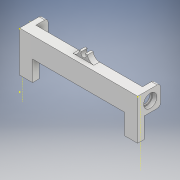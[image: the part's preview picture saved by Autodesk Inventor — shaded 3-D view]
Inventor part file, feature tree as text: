
AUTODESK INVENTOR PART (.ipt)
format: ipt  version: 2018 (Build 220112000, 112)  size: 1,079,296 bytes
history: native  units: mm
features: sketch x60, extrude x49, fillet x5
ambient origin geometry x8: Origin, YZ Plane, XZ Plane, XY Plane, X Axis, Y Axis, Z Axis, Center Point
bodies: Solid1 (feature_tree)
feature tree (114):
  extrude  "Extrusion1"  Depth=80.0mm
  extrude  "Extrusion2"  Depth=3.0mm
  sketch  "Sketch3"  dims[d5=12.0mm d6=14.5mm]
  extrude  "Extrusion3"  Depth=14.5mm
  extrude  "Extrusion4"  Depth=2.0mm
  extrude  "Extrusion5"  Depth=0.5mm TaperAngle=0.0deg
  sketch  "Sketch7"  dims[d15=10.0mm d16=25.0mm]
  extrude  "Extrusion6"  Depth=25.0mm
  extrude  "Extrusion7"  Depth=25.0mm
  extrude  "Extrusion8"  Depth=10.0mm
  fillet  "Fillet1"  Radius=10.0mm
  fillet  "Fillet2"  Radius=10.0mm
  extrude  "Extrusion9"  Depth=2.5mm TaperAngle=0.0deg
  extrude  "Extrusion10"  Depth=4.0mm
  fillet  "Fillet3"  Radius=3.0mm
  extrude  "Extrusion11"  Depth=21.0mm
  extrude  "Extrusion12"  Depth=41.0mm
  extrude  "Extrusion13"  Depth=42.0mm
  extrude  "Extrusion14"  Depth=38.0mm
  extrude  "Extrusion15"  Depth=45.0mm TaperAngle=0.0deg
  extrude  "Extrusion16"  Depth=3.0mm TaperAngle=0.0deg
  extrude  "Extrusion17"  Depth=3.0mm
  extrude  "Extrusion18"  Depth=39.5mm
  extrude  "Extrusion19"  Depth=7.25mm
  extrude  "Extrusion20"  Depth=7.75mm
  extrude  "Extrusion21"  Depth=10.0mm
  sketch  "Sketch24"  dims[d65=66.0mm d66=3.5mm d67=0.0mm]
  extrude  "Extrusion22"  Depth=10.0mm TaperAngle=0.0deg
  extrude  "Extrusion23"  Depth=16.0mm
  extrude  "Extrusion24"  Depth=3.5mm TaperAngle=0.0deg
  extrude  "Extrusion25"  Depth=2.0mm
  extrude  "Extrusion26"  Depth=2.0mm TaperAngle=0.0deg
  sketch  "Sketch30"  dims[d81=4.0mm d82=4.0mm]
  extrude  "Extrusion27"  Depth=16.0mm
  extrude  "Extrusion28"  Depth=2.0mm
  extrude  "Extrusion29"  Depth=3.5mm TaperAngle=0.0deg
  sketch  "Sketch34"  dims[d91=5.0mm d92=16.0mm d93=5.0mm]
  extrude  "Extrusion30"  Depth=4.0mm
  extrude  "Extrusion31"  Depth=2.0mm TaperAngle=0.0deg
  extrude  "Extrusion32"  Depth=150.0mm TaperAngle=0.0deg
  sketch  "Sketch38"  dims[d102=5.0mm d103=0.0mm d104=500.0mm d105=0.0mm]
  extrude  "Extrusion33"  Depth=16.0mm
  sketch  "Sketch40"  dims[d110=38.75mm d111=38.75mm]
  extrude  "Extrusion34"  Depth=16.0mm
  fillet  "Fillet4"  Radius=5.0mm
  extrude  "Extrusion35"  Depth=3.0mm
  extrude  "Extrusion36"  Depth=43.0mm TaperAngle=0.0deg
  extrude  "Extrusion37"  Depth=38.75mm
  extrude  "Extrusion38"  Depth=5.0mm TaperAngle=0.0deg
  extrude  "Extrusion39"  Depth=45.0mm TaperAngle=0.0deg
  extrude  "Extrusion40"  Depth=38.75mm
  sketch  "Sketch48"  dims[d134=16.0mm d135=5.0mm d136=0.0mm d137=7.0mm]
  extrude  "Extrusion41"  Depth=3.5mm TaperAngle=0.0deg
  extrude  "Extrusion42"  Depth=100.0mm TaperAngle=0.0deg
  extrude  "Extrusion43"  Depth=1.5mm TaperAngle=0.0deg
  sketch  "Sketch52"  dims[d144=16.0mm]
  extrude  "Extrusion44"  Depth=10.0mm
  extrude  "Extrusion45"  Depth=10.0mm
  extrude  "Extrusion46"  Depth=7.0mm
  sketch  "Sketch56"  dims[d150=5.0mm d151=0.0mm]
  sketch  "Sketch57"  dims[d152=5.0mm d153=0.0mm]
  extrude  "Extrusion47"  Depth=7.75mm
  extrude  "Extrusion48"  Depth=5.0mm TaperAngle=0.0deg
  fillet  "Fillet5"  Radius=7.0mm
  extrude  "Extrusion49"  Depth=15.0mm TaperAngle=0.0deg
  sketch  "Sketch1"  dims[d0=145.0mm d1=80.0mm]
  sketch  "Sketch2"  dims[d2=3.0mm d3=0.0mm d4=12.0mm]
  sketch  "Sketch4"  dims[d7=2.0mm d8=2.0mm]
  sketch  "Sketch5"  dims[d9=6.0mm d10=0.0mm d11=0.5mm d12=0.0mm]
  sketch  "Sketch6"  dims[d13=10.0mm d14=25.0mm]
  sketch  "Sketch8"  dims[d17=25.0mm d18=0.0mm d19=22.5mm d20=10.0mm d21=0.0mm d22=10.0mm]
  sketch  "Sketch9"  dims[d23=2.5mm d24=0.0mm d25=7.5mm d26=0.0mm]
  sketch  "Sketch10"  dims[d27=10.0mm d28=0.0mm d29=4.0mm d30=3.0mm]
  sketch  "Sketch11"  dims[d31=1.0mm d32=21.0mm]
  sketch  "Sketch12"  dims[d33=38.0mm d34=41.0mm]
  sketch  "Sketch13"  dims[d35=38.0mm d36=42.0mm]
  sketch  "Sketch14"  dims[d37=41.0mm d38=38.0mm]
  sketch  "Sketch15"  dims[d39=42.0mm d40=45.0mm d41=0.0mm]
  sketch  "Sketch16"  dims[d42=12.5mm d43=3.0mm d44=0.0mm]
  sketch  "Sketch17"  dims[d45=3.0mm d46=39.5mm]
  sketch  "Sketch18"  dims[d47=39.5mm d48=39.5mm]
  sketch  "Sketch19"  dims[d49=45.0mm d50=0.0mm d51=7.25mm]
  sketch  "Sketch20"  dims[d52=4.0mm d53=7.75mm d54=0.0mm d55=0.0mm d56=125.0mm]
  sketch  "Sketch21"  dims[d57=10.0mm d58=0.0mm d59=1.0mm]
  sketch  "Sketch22"  dims[d60=14.5mm d61=10.0mm d62=0.0mm]
  sketch  "Sketch23"  dims[d63=16.0mm d64=12.0mm]
  sketch  "Sketch25"  dims[d68=4.0mm d69=2.0mm]
  sketch  "Sketch26"  dims[d70=4.0mm d71=2.0mm d72=0.0mm]
  sketch  "Sketch27"  dims[d73=2.0mm d74=0.0mm d75=16.0mm]
  sketch  "Sketch28"  dims[d76=2.0mm d77=2.0mm]
  sketch  "Sketch29"  dims[d78=2.0mm d79=3.5mm d80=0.0mm]
  sketch  "Sketch31"  dims[d83=4.0mm d84=2.0mm d85=0.0mm]
  sketch  "Sketch32"  dims[d86=15.5mm d87=150.0mm d88=0.0mm]
  sketch  "Sketch33"  dims[d89=12.0mm d90=16.0mm]
  sketch  "Sketch35"  dims[d94=12.0mm d95=3.0mm]
  sketch  "Sketch36"  dims[d96=43.0mm d97=0.0mm d98=43.0mm d99=0.0mm]
  sketch  "Sketch37"  dims[d100=38.75mm d101=38.75mm]
  sketch  "Sketch39"  dims[d106=45.0mm d107=0.0mm d108=45.0mm d109=0.0mm]
  sketch  "Sketch41"  dims[d112=45.0mm d113=0.0mm d114=3.5mm d115=0.0mm]
  sketch  "Sketch42"  dims[d116=43.0mm d117=0.0mm d118=100.0mm d119=0.0mm]
  sketch  "Sketch43"  dims[d120=200.0mm d121=0.0mm d122=1.5mm d123=0.0mm]
  sketch  "Sketch44"  dims[d124=5.0mm d125=10.0mm]
  sketch  "Sketch45"  dims[d126=10.0mm d127=6.35mm]
  sketch  "Sketch46"  dims[d128=7.0mm d129=0.0mm d130=2.75mm]
  sketch  "Sketch47"  dims[d131=7.0mm d132=0.0mm d133=7.75mm]
  sketch  "Sketch49"  dims[d138=7.0mm d139=15.0mm d140=0.0mm]
  sketch  "Sketch50"  dims[d141=13.5mm]
  sketch  "Sketch51"  dims[d142=2.0mm d143=0.0mm]
  sketch  "Sketch53"  dims[d145=5.0mm d146=0.0mm]
  sketch  "Sketch54"  dims[d147=2.0mm d148=0.0mm]
  sketch  "Sketch55"  dims[d149=16.25mm]
  sketch  "Sketch58"  dims[d154=3.0mm d155=0.0mm]
  sketch  "Sketch59"  dims[d156=3.0mm d157=0.0mm]
  sketch  "Sketch60"  dims[d158=12.25mm d159=3.5mm d160=43.0mm d161=0.0mm d162=12.25mm d163=3.5mm d164=43.0mm d165=0.0mm d166=18.0mm d167=43.0mm d168=0.0mm d169=131.0mm d170=0.0mm d171=131.0mm d172=0.0mm d173=0.5mm d174=2.0mm d175=0.0mm]
